# Revit family: 60-E082-Z5-CM
name_source: partatom
category: Luminarias
revit_build: Autodesk Revit 2017 (Build: 20160225_1515(x64)
units: mm (PartAtom-declared; Revit-internal decimal feet)

## family parameters
Compartido = Sí
Corte con vacíos al cargar = No
Cota de conector redondo = Diámetro de uso
Número OmniClass = 23.80.70.00
Origen de luz = No
Punto de cálculo de habitación = No
Se basa en plano de trabajo = No
Siempre vertical = Sí
Tipo de pieza = Normal
Título OmniClass = Lighting

## types (1)
- 60-E082-Z5-CM
    Acabado = Transparente
    CRI = 80
    Catálogo = Outdoor
    CodigoGubimclass = 50.60.50.20
    CodigoOmniclass = 21-04 50 40
    CodigoUniclass2015 = EF_70_80
    CodigoUniformat2010 = D5040
    DescripcionGubimclass = Iluminación interior
    DescripcionOmniclass = Lighting
    DescripcionUniclass2015 = Lighting
    DescripcionUniformat2010 = Lighting
    EAN13 = 8435575323841
    Eficiencia energética = LED A++
    Etiqueta V/f = 100-277V/50-60Hz
    Fabricante = LEDS C4
    Familia = Proud Asymmetrical Head
    FechaVersion = Julio 2020
    Ficha = http://files.leds-c4.com
    Fotometría = http://files.leds-c4.com
    IK = IK10
    IMC = http://files.leds-c4.com
    IP = IP65
    IfcExportAs = IfcLightFixture
    IfcExportType = NOTDEFINED
    LDT = http://files.leds-c4.com
    Lumenes reales (lm) = 5227
    Material = Aluminio, Policarbonato
    Peso neto (KG) = 0
    Producto descatalogado = Catalogado ES
    Rayo de luz = Check Photometric file
    Referencia = 60-E082-Z5-CM
    Temperatura color led (K) = Blanco neutro - 4000K
    Tender text (Castellano) = LEDS C4
Proud Asymmetrical Head
60-E082-Z5-CM

Cabezal de uso exterior para iluminar hacia abajo. 
Apto para instalar en ambientes con atmósfera marina. Metros cable incluido: 0.4. Material estructura: Aluminio. Material difusor: Policarbonato. Acabado difusor: Transparente. Protección contra los rayos ultravioleta. Garantía: 5 Años. Ta max: 50ºC.

Peso neto del producto (Kg): 0.000
Anchura o diámetro del producto (mm): 440
Altura del producto (mm): 466
Diámetro (mm) admitido del poste en instalación vertical: 60

Clase 1. IP: IP65. IK: IK10. LED. Nº de portalámparas o Leds: 80. Marca del LED: CREE. Marca del Driver: SOSEN. Potencia máxima de la fuente de luz: 44W. Temperatura de color: Blanco neutro - 4000K. Índice de reproducción cromática: 80. Steps Mac Adam: 3. Diámetro máximo de la bombilla que admite la luminaria: 50.000h L80B20. UGR:  21.2. Riesgo fotobiológico: RG1. % de Flickering: &lt;5%. Flujo real (lm): 5227. Lm/W reales: 113. Rango de voltaje/frecuencia: 90-305/50-60Hz. Voltaje: 3.2. Equipo incluido: Si, electrónico. Potencia total: 46.4. Factor de potencia: 0.96. Equipo regulable incluido: 0-10V.
    Tender text (English) = LEDS C4
Proud Asymmetrical Head
60-E082-Z5-CM

Head for outdoor use. 

For downlighting. Suitable for installation in marine environments. Cable meters included: 0.4. Structure material: Aluminium. Diffuser material: Polycarbonate. Diffuser finish: Transparent. UV protection. Warranty: 5 Years. Ta max: 50ºC.

Product net weight (Kg): 0.000
Product width or diameter (mm): 440
Product height (mm): 466
Permitted post diameter (mm) for vertical installation: 60

Class 1. IP: IP65. IK: IK10. LED. No. of lampholders or LEDs: 80. LED brand: CREE. Driver brand: SOSEN. Maximum power of light source: 44W. Colour temperature: LED neutral-white 4000K. Colour rendering index: 80. MacAdam Steps: 3. Maximum diameter of luminaire bulb: 50.000h L80B20. UGR:  21.2. Photobiological risk: RG1. % de Flickering: &lt;5%. Real flux (lm): 5227. Lm/Real W: 113. Voltage and frequency range: 90-305/50-60Hz. Voltage: 3.2. Gear included: Yes, electronic. Total power: 46.4. Power factor: 0.96. Dimmable gear included: 0-10V.
    Tipo = Farola
    Tipo de regulación = 0-10V
    Vatios (W) = 46.4
    Versión = v1
